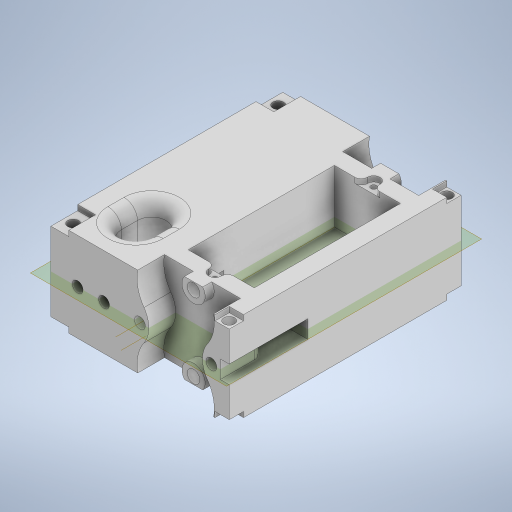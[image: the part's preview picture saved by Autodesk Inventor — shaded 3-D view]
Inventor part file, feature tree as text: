
AUTODESK INVENTOR PART (.ipt)
format: ipt  version: 2024.2 (Build 282272000, 272)  size: 1,146,880 bytes
history: native  units: in
note: dims shown in document units (in); Inventor stores cm internally (conversion verified against a paired STEP export)
features: sketch x29, extrude x27, mirror x14, projected_geometry x10, plane x4, chamfer x3, other x2, fillet x2, revolve x1
ambient origin geometry x8: Origin, YZ Plane, XZ Plane, XY Plane, X Axis, Y Axis, Z Axis, Center Point
bodies: Solid1 (feature_tree)
feature tree (92):
  extrude  "Extrusion1"  Depth=3.937in
  extrude  "Extrusion2"  Depth=0.5906in TaperAngle=0.0deg
  sketch  "Sketch3"  dims[d8=0.2913in d11=0.0472in]
  sketch  "Sketch4"  dims[d12=0.0472in d13=0.253in]
  plane  "Work Plane1"
  mirror  "Mirror1"
  extrude  "Extrusion5"  Depth=0.0472in
  extrude  "Extrusion6"  Depth=0.253in
  chamfer  "Chamfer1"  Distance=1.063in
  chamfer  "Chamfer2"  Distance=0.315in
  chamfer  "Chamfer3"  Distance=0.0787in Angle=45.0deg
  extrude  "Extrusion7"  Depth=0.0787in TaperAngle=45.0deg
  extrude  "Extrusion9"  Depth=3.2283in
  extrude  "Extrusion10"  Depth=0.2756in
  sketch  "Sketch11"  dims[d24=0.0984in]
  extrude  "Extrusion11"  Depth=0.1378in
  sketch  "Sketch13"  dims[d25=0.0984in]
  other  "Work Axis2"
  revolve  "Revolution1"  [1 undecoded]
  extrude  "Extrusion12"  Depth=0.1969in
  extrude  "Extrusion13"  Depth=0.1181in
  extrude  "Extrusion14"  Depth=0.1969in TaperAngle=0.0deg
  mirror  "Mirror2"
  plane  "Work Plane3"
  extrude  "Extrusion15"  Depth=0.7874in
  plane  "Work Plane4"
  extrude  "Extrusion16"  Depth=0.3937in
  extrude  "Extrusion18"  TaperAngle=225.0deg  [1 undecoded]
  extrude  "Extrusion19"  Depth=0.1969in
  extrude  "Extrusion20"  Depth=0.1969in
  fillet  "Fillet4"  Radius=0.1969in
  sketch  "Sketch25"  dims[d39=0.1181in d40=0.0787in d41=0.315in d42=45.0deg]
  extrude  "Extrusion21"  Depth=0.7874in
  extrude  "Extrusion22"  Depth=0.3937in
  mirror  "Mirror4"
  other  "Work Axis3"
  extrude  "Extrusion23"  Depth=0.1969in TaperAngle=0.0deg
  plane  "Work Plane2"
  mirror  "Mirror6"
  extrude  "Extrusion24"  Depth=0.2362in
  mirror  "Mirror7"
  extrude  "Extrusion25"  Depth=0.5906in
  mirror  "Mirror8"
  mirror  "Mirror9"
  mirror  "Mirror10"
  sketch  "Sketch29"  dims[d62=0.1378in d63=0.1378in]
  extrude  "Extrusion28"  Depth=0.3937in TaperAngle=0.0deg
  mirror  "Mirror13"
  mirror  "Mirror14"
  sketch  "Sketch32"  dims[d67=0.1969in d68=0.1969in]
  extrude  "Extrusion29"  Depth=0.1969in
  extrude  "Extrusion30"  Depth=0.1969in
  mirror  "Mirror15"
  mirror  "Mirror16"
  extrude  "Extrusion31"  Depth=0.3937in TaperAngle=0.0deg
  extrude  "Extrusion32"  Depth=0.7874in
  extrude  "Extrusion33"  Depth=1.1811in
  mirror  "Mirror17"
  mirror  "Mirror18"
  fillet  "Fillet5"  Radius=0.2362in
  sketch  "Sketch1"  dims[d0=5.1181in d1=3.937in]
  sketch  "Sketch2"  dims[d2=1.9685in d3=0.0in d4=0.5906in d5=0.0in]
  projected_geometry  "Projected Loop1"
  projected_geometry  "Projected Loop2"
  sketch  "Sketch5"  dims[d14=0.253in]
  sketch  "Sketch6"  dims[d18=0.1575in]
  sketch  "Sketch7"  dims[d19=1.6535in]
  sketch  "Sketch9"  dims[d20=3.7402in d21=1.063in d22=0.0in]
  sketch  "Sketch10"  dims[d23=0.0984in]
  projected_geometry  "Projected Loop3"
  projected_geometry  "Projected Loop4"
  sketch  "Sketch15"  dims[d26=1.3465in]
  projected_geometry  "Projected Loop5"
  projected_geometry  "Projected Loop6"
  sketch  "Sketch16"  dims[d28=2.126in]
  sketch  "Sketch17"  dims[d30=1.3465in d32=0.315in d33=0.0in]
  sketch  "Sketch18"  dims[d34=0.1181in]
  sketch  "Sketch19"  dims[d35=0.1181in]
  projected_geometry  "Projected Loop7"
  projected_geometry  "Projected Loop8"
  sketch  "Sketch21"  dims[d36=0.1181in]
  sketch  "Sketch22"  dims[d37=0.1181in]
  projected_geometry  "Projected Loop9"
  sketch  "Sketch23"  dims[d38=0.1181in]
  sketch  "Sketch26"  dims[d43=0.0787in d44=0.315in d45=45.0deg d46=0.0787in d47=0.315in d48=45.0deg]
  projected_geometry  "Projected Loop10"
  sketch  "Sketch27"  dims[d49=1.4567in d50=3.2283in]
  sketch  "Sketch28"  dims[d52=1.1811in d53=0.0in d60=0.2756in]
  sketch  "Sketch31"  dims[d64=0.1181in d65=0.0in d66=0.3937in]
  sketch  "Sketch33"  dims[d69=0.1181in d70=0.0in d71=0.122in]
  sketch  "Sketch34"  dims[d72=0.122in d73=0.1969in d74=0.0in]
  sketch  "Sketch35"  dims[d75=0.3937in d76=0.7874in d77=0.3937in d78=225.0deg d79=0.122in d80=0.122in d81=0.1969in d82=0.0in d83=0.7874in d84=0.3937in d85=0.1969in d86=0.0in d87=0.2362in d88=0.5906in d89=0.3937in d90=0.0in d91=1.378in d92=1.378in d93=0.3937in d94=0.0in d95=0.7874in d96=1.1811in d97=0.2362in d99=0.3937in d100=0.0in d101=0.2362in d102=0.1969in d108=0.6299in d109=0.3543in d110=0.1969in d111=0.5118in d112=0.0in d114=0.7874in d115=0.0in d116=0.1063in d117=0.1063in d118=0.0906in d119=0.0906in d120=0.1575in d121=0.0in d128=0.2953in d129=0.5906in d130=0.3937in d131=0.2953in d132=0.2362in d133=0.1969in d134=0.1181in d135=0.0in d136=0.1969in d137=0.0in d138=0.1969in d139=0.0in d140=0.3937in d141=2.5591in d142=0.3937in d143=0.0in d144=0.1969in d145=0.2362in d146=0.5827in d147=0.7874in d148=0.8268in d149=0.2756in d150=0.1181in d151=0.1969in d152=0.0in d161=1.1811in d162=0.0in d163=0.3937in d164=0.0in d165=0.3937in d166=0.0in d167=0.3937in d168=0.1969in d169=0.0in d170=0.315in d171=0.315in d172=0.1181in d173=0.0in d174=0.2362in d175=0.1575in d176=0.1575in d177=0.4331in d178=0.0in d179=0.1969in d103=0.0197in d104=0.0344in d105=0.0197in d106=0.0344in d127=0.0in]
note: 2 required parameter values undecoded (feature->parameter linkage not recoverable at this tier; creation-order binding heuristic only, values carry confidence <= 0.55)